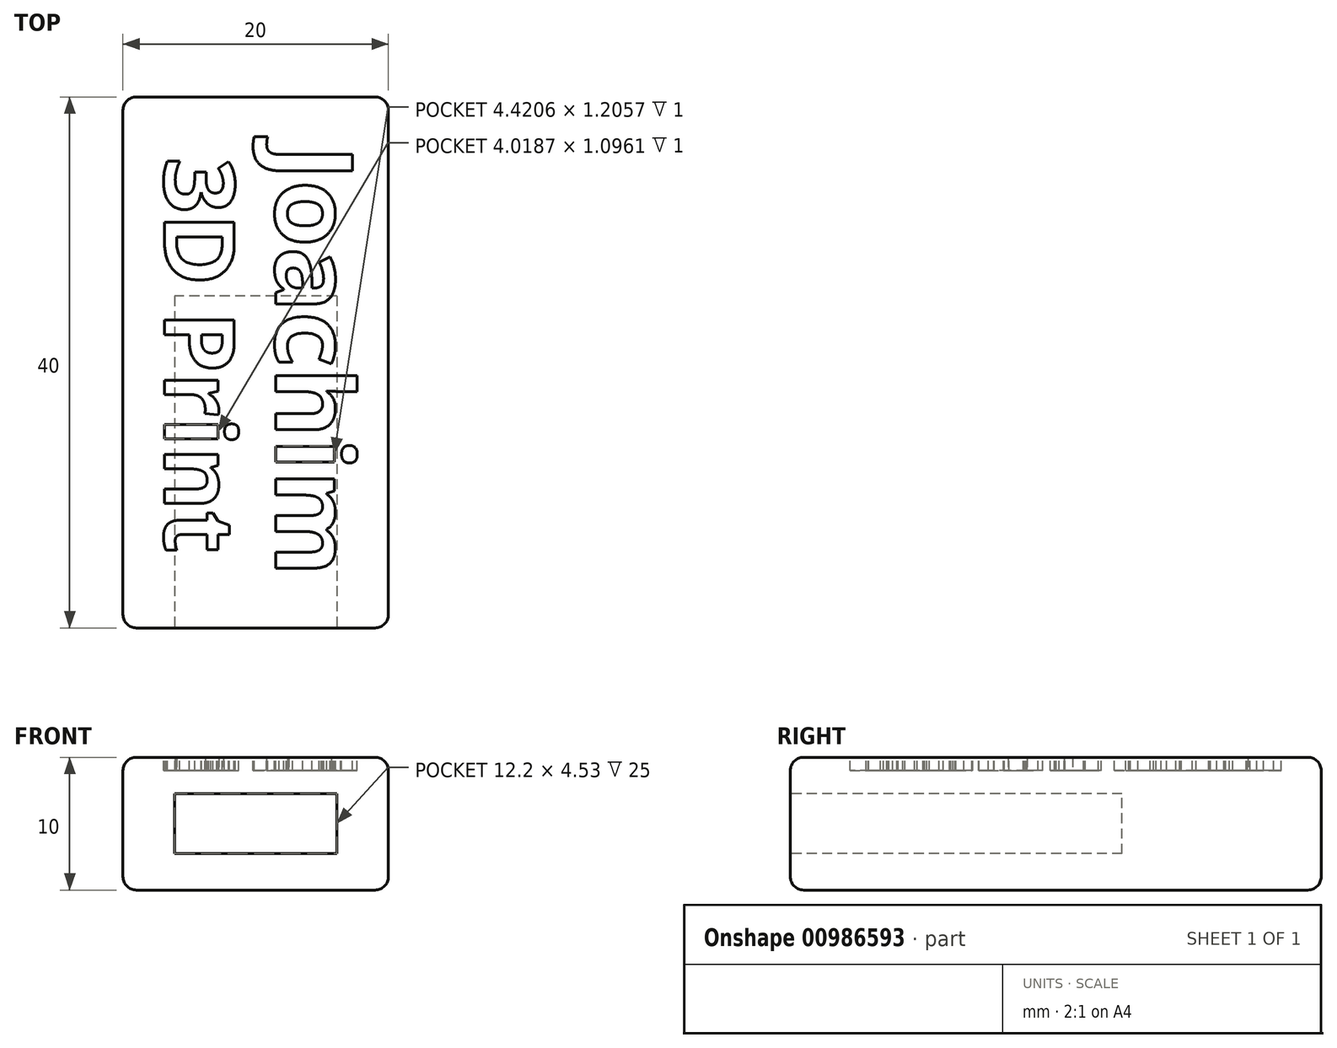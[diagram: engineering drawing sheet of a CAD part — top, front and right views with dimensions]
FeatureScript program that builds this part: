
annotation { "Feature Type Name" : "Feature", "Feature Type Description" : "" }
export const myFeature = defineFeature(function(context is Context, id is Id, definition is map)
    precondition{}
    {
        {
            var Q0;
            Q0=qCreatedBy(makeId("Front.planeOp"),FACE);
            var sketch = newSketch(context, id + "F0", { "sketchPlane" : qUnion([Q0])});
            skLineSegment(sketch, "E0.bottom", {"start": v(10, -5) * mm, "end": v(-10, -5) * mm});
            skLineSegment(sketch, "E0.top", {"start": v(10, 5) * mm, "end": v(-10, 5) * mm});
            skLineSegment(sketch, "E0.left", {"start": v(10, -5) * mm, "end": v(10, 5) * mm});
            skLineSegment(sketch, "E0.right", {"start": v(-10, -5) * mm, "end": v(-10, 5) * mm});
            skPoint(sketch, "E0.middle", {"position": v(0, 0) * mm});
            skSolve(sketch);
        }
        {
            var Q0;
            Q0=qCreatedBy(makeId("Front.planeOp"),FACE);
            var sketch = newSketch(context, id + "F1", { "sketchPlane" : qUnion([Q0])});
            skLineSegment(sketch, "E1.bottom", {"start": v(6.1, -2.27) * mm, "end": v(-6.1, -2.27) * mm});
            skLineSegment(sketch, "E1.top", {"start": v(6.1, 2.26) * mm, "end": v(-6.1, 2.26) * mm});
            skLineSegment(sketch, "E1.left", {"start": v(6.1, -2.27) * mm, "end": v(6.1, 2.26) * mm});
            skLineSegment(sketch, "E1.right", {"start": v(-6.1, -2.27) * mm, "end": v(-6.1, 2.26) * mm});
            skPoint(sketch, "E1.middle", {"position": v(0, 0) * mm});
            skSolve(sketch);
        }
        {
            var Q0;
            Q0=makeQuery(id+"F0.imprint","IMPRINT",FACE,{"disambiguationData":[TD([[makeQuery(id+"F0.imprint","IMPRINT",EDGE,{"derivedFrom":sQuery(id+"F0.wireOp",EDGE,"E0.bottom")}),-1.0]])]});
            extrude(context, id + "F2", {"entities" : qUnion([Q0]), "oppositeDirection" : true, "depth" : 40 * mm, "offsetDistance" : 25 * mm});
        }
        {
            var Q0;
            Q0 = qSketchRegion(id + "F1", true);
            extrude(context, id + "F3", {"entities" : qUnion([Q0]), "operationType" : NewBodyOperationType.REMOVE, "oppositeDirection" : true, "depth" : 25 * mm, "offsetDistance" : 25 * mm});
        }
        {
            var Q0;
            Q0=makeQuery(id+"F2.opExtrude","SWEPT_EDGE",EDGE,{"disambiguationData":[OSD([sQuery(id+"F0.wireOp",EDGE,"E0.top"),sQuery(id+"F0.wireOp",EDGE,"E0.left")])]});
            var Q1;
            Q1=makeQuery(id+"F2.opExtrude","CAP_EDGE",EDGE,{"disambiguationData":[OSD([sQuery(id+"F0.wireOp",EDGE,"E0.top")])],"isStart":false});
            var Q2;
            Q2=makeQuery(id+"F2.opExtrude","SWEPT_EDGE",EDGE,{"disambiguationData":[OSD([sQuery(id+"F0.wireOp",EDGE,"E0.top"),sQuery(id+"F0.wireOp",EDGE,"E0.right")])]});
            var Q3;
            Q3=makeQuery(id+"F2.opExtrude","SWEPT_EDGE",EDGE,{"disambiguationData":[OSD([sQuery(id+"F0.wireOp",EDGE,"E0.bottom"),sQuery(id+"F0.wireOp",EDGE,"E0.right")])]});
            var Q4;
            Q4=makeQuery(id+"F2.opExtrude","CAP_EDGE",EDGE,{"disambiguationData":[OSD([sQuery(id+"F0.wireOp",EDGE,"E0.right")])],"isStart":false});
            var Q5;
            Q5=makeQuery(id+"F2.opExtrude","CAP_EDGE",EDGE,{"disambiguationData":[OSD([sQuery(id+"F0.wireOp",EDGE,"E0.bottom")])],"isStart":true});
            var Q6;
            Q6=makeQuery(id+"F2.opExtrude","CAP_EDGE",EDGE,{"disambiguationData":[OSD([sQuery(id+"F0.wireOp",EDGE,"E0.top")])],"isStart":true});
            var Q7;
            Q7=makeQuery(id+"F2.opExtrude","CAP_EDGE",EDGE,{"disambiguationData":[OSD([sQuery(id+"F0.wireOp",EDGE,"E0.left")])],"isStart":true});
            var Q8;
            Q8=makeQuery(id+"F2.opExtrude","SWEPT_EDGE",EDGE,{"disambiguationData":[OSD([sQuery(id+"F0.wireOp",EDGE,"E0.bottom"),sQuery(id+"F0.wireOp",EDGE,"E0.left")])]});
            var Q9;
            Q9=makeQuery(id+"F2.opExtrude","CAP_EDGE",EDGE,{"disambiguationData":[OSD([sQuery(id+"F0.wireOp",EDGE,"E0.bottom")])],"isStart":false});
            var Q10;
            Q10=makeQuery(id+"F2.opExtrude","CAP_EDGE",EDGE,{"disambiguationData":[OSD([sQuery(id+"F0.wireOp",EDGE,"E0.left")])],"isStart":false});
            var Q11;
            Q11=makeQuery(id+"F2.opExtrude","CAP_EDGE",EDGE,{"disambiguationData":[OSD([sQuery(id+"F0.wireOp",EDGE,"E0.right")])],"isStart":true});
            fillet(context, id + "F4", {"entities" : qUnion([Q0, Q1, Q2, Q3, Q4, Q5, Q6, Q7, Q8, Q9, Q10, Q11]), "radius" : 1 * mm, "tangentPropagation" : true, "allowEdgeOverflow" : false});
        }
        {
            var Q0;
            Q0=makeQuery(id+"F2.opExtrude","SWEPT_FACE",FACE,{"disambiguationData":[OSD([sQuery(id+"F0.wireOp",EDGE,"E0.top")])]});
            var sketch = newSketch(context, id + "F5", { "sketchPlane" : qUnion([Q0])});
            skText(sketch, "E2", { "text": "Joachim", "fontName": "OpenSans-Bold.ttf"});
            const initialGuessF5  = {"E2": [0.0015, 0.03639, 0, -1, 0.00583]};
            skSetInitialGuess(sketch, initialGuessF5);
            skSolve(sketch);
        }
        {
            var Q0;
            Q0 = qSketchRegion(id + "F5", true);
            extrude(context, id + "F6", {"entities" : qUnion([Q0]), "operationType" : NewBodyOperationType.REMOVE, "oppositeDirection" : true, "depth" : 1 * mm, "offsetDistance" : 25 * mm});
        }
        {
            var Q0;
            {var subQ1=sQuery(id+"F0.wireOp",EDGE,"E0.top");Q0=makeQuery(id+"F6.boolean.opBoolean","SPLIT",FACE,{"disambiguationData":[TD([makeQuery(id+"F6.opExtrude","SWEPT_FACE",FACE,{"disambiguationData":[OSD([sQuery(id+"F5.wireOp",EDGE,"E2.sketch_text.stroke-0")])]})])],"derivedFrom":makeQuery(id+"F2.opExtrude","SWEPT_FACE",FACE,{"disambiguationData":[OSD([subQ1])]})});}
            var sketch = newSketch(context, id + "F7", { "sketchPlane" : qUnion([Q0])});
            skText(sketch, "E3", { "text": "3D Print", "fontName": "OpenSans-Bold.ttf"});
            const initialGuessF7  = {"E3": [-0.00687, 0.03543, 0, -1, 0.0053]};
            skSetInitialGuess(sketch, initialGuessF7);
            skSolve(sketch);
        }
        {
            var Q0;
            Q0 = qSketchRegion(id + "F7", true);
            extrude(context, id + "F8", {"entities" : qUnion([Q0]), "operationType" : NewBodyOperationType.REMOVE, "oppositeDirection" : true, "depth" : 1 * mm, "offsetDistance" : 25 * mm});
        }
    });
